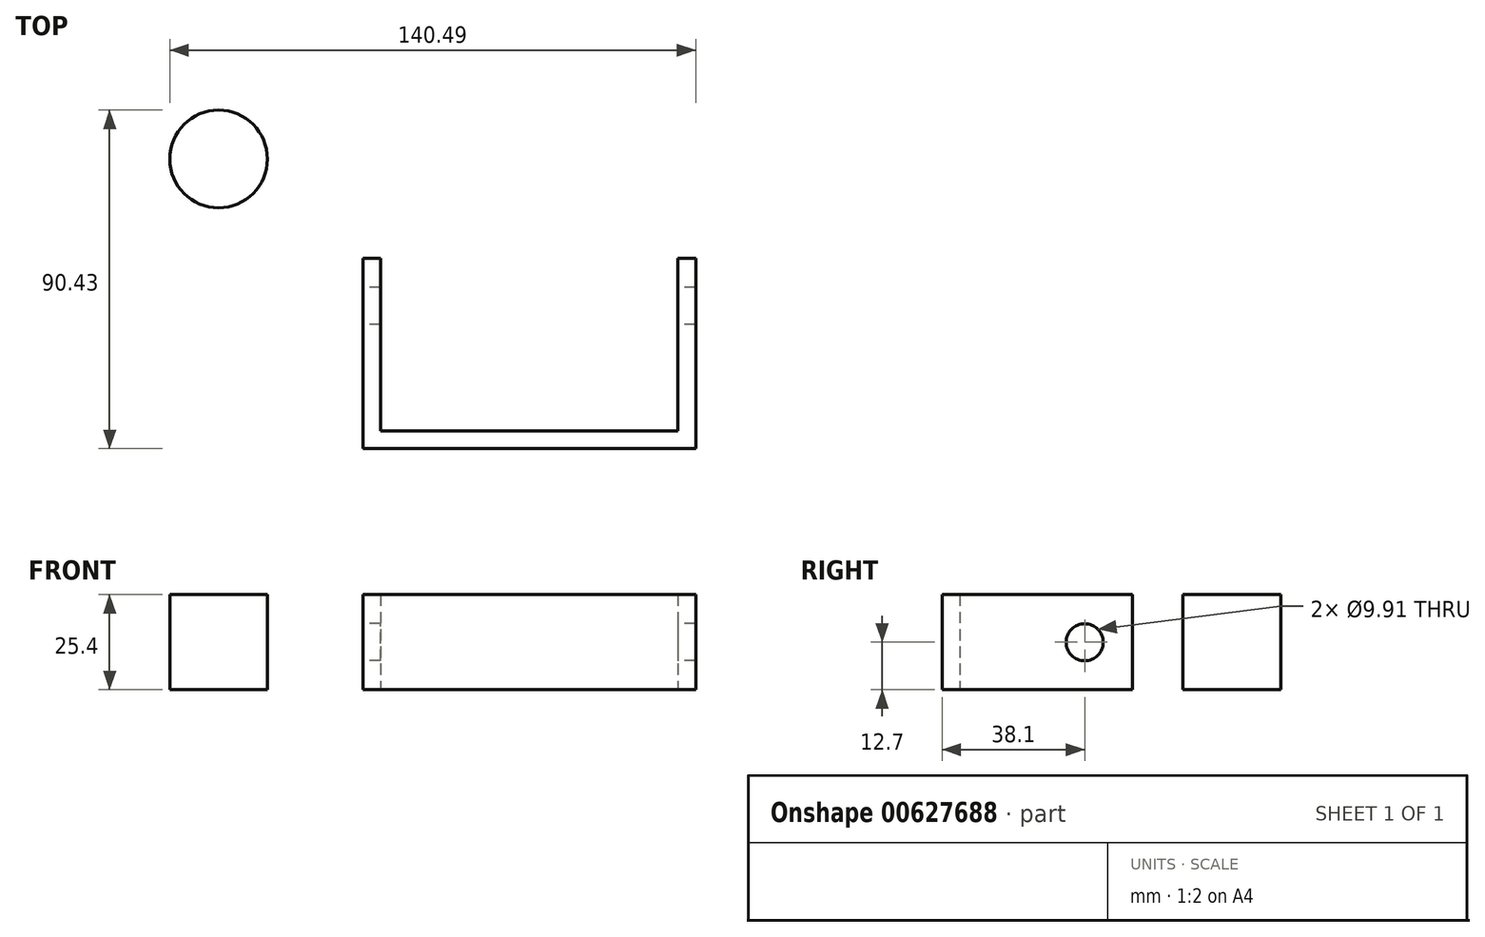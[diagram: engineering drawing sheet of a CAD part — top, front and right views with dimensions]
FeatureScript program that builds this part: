
annotation { "Feature Type Name" : "Feature", "Feature Type Description" : "" }
export const myFeature = defineFeature(function(context is Context, id is Id, definition is map)
    precondition{}
    {
        {
            var Q0;
            Q0=qCreatedBy(makeId("Top.planeOp"),FACE);
            var sketch = newSketch(context, id + "F0", { "sketchPlane" : qUnion([Q0])});
            skLineSegment(sketch, "E0.bottom", {"start": v(44.45, 0) * mm, "end": v(-44.45, 0) * mm});
            skLineSegment(sketch, "E0.top", {"start": v(44.45, 50.8) * mm, "end": v(-44.45, 50.8) * mm, "construction": true});
            skLineSegment(sketch, "E0.left", {"start": v(44.45, 0) * mm, "end": v(44.45, 50.8) * mm});
            skLineSegment(sketch, "E0.right", {"start": v(-44.45, 0) * mm, "end": v(-44.45, 50.8) * mm});
            skPoint(sketch, "E0.middle", {"position": v(0, 25.4) * mm});
            skLineSegment(sketch, "E1", {"start": v(-44.45, 38.1) * mm, "end": v(44.45, 38.1) * mm, "construction": true});
            skLineSegment(sketch, "E2.bottom", {"start": v(-38.1, 63.5) * mm, "end": v(38.1, 63.5) * mm, "construction": true});
            skLineSegment(sketch, "E2.top", {"start": v(-38.1, 12.7) * mm, "end": v(38.1, 12.7) * mm, "construction": true});
            skLineSegment(sketch, "E2.left", {"start": v(-38.1, 63.5) * mm, "end": v(-38.1, 12.7) * mm, "construction": true});
            skLineSegment(sketch, "E2.right", {"start": v(38.1, 63.5) * mm, "end": v(38.1, 12.7) * mm, "construction": true});
            skPoint(sketch, "E2.middle", {"position": v(0, 38.1) * mm});
            skLineSegment(sketch, "E3", {"start": v(-44.45, 50.8) * mm, "end": v(-39.69, 50.8) * mm});
            skLineSegment(sketch, "E4", {"start": v(-39.69, 50.8) * mm, "end": v(-39.69, 4.76) * mm});
            skLineSegment(sketch, "E5", {"start": v(-39.69, 4.76) * mm, "end": v(39.69, 4.76) * mm});
            skLineSegment(sketch, "E6", {"start": v(39.69, 4.76) * mm, "end": v(39.69, 50.8) * mm});
            skLineSegment(sketch, "E7", {"start": v(39.69, 50.8) * mm, "end": v(44.45, 50.8) * mm});
            skSolve(sketch);
        }
        {
            var Q0;
            Q0 = qSketchRegion(id + "F0", true);
            extrude(context, id + "F1", {"entities" : qUnion([Q0]), "depth" : 25.4 * mm, "offsetDistance" : 25.4 * mm});
        }
        {
            var Q0;
            Q0=makeQuery(id+"F1.opExtrude","SWEPT_FACE",FACE,{"disambiguationData":[OSD([sQuery(id+"F0.wireOp",EDGE,"E0.right")])]});
            var sketch = newSketch(context, id + "F2", { "sketchPlane" : qUnion([Q0])});
            skLineSegment(sketch, "E8", {"start": v(0, 12.7) * mm, "end": v(-50.8, 12.7) * mm, "construction": true});
            skCircle(sketch, "E9", {"center": v(-38.1, 12.7) * mm, "radius": 4.95 * mm});
            skSolve(sketch);
        }
        {
            var Q0;
            Q0 = qSketchRegion(id + "F2", true);
            extrude(context, id + "F3", {"entities" : qUnion([Q0]), "operationType" : NewBodyOperationType.REMOVE, "endBound" : BoundingType.THROUGH_ALL, "oppositeDirection" : true, "depth" : 25.4 * mm, "offsetDistance" : 25.4 * mm});
        }
        {
            var Q0;
            Q0=qCreatedBy(makeId("Top.planeOp"),FACE);
            var sketch = newSketch(context, id + "F4", { "sketchPlane" : qUnion([Q0])});
            skCircle(sketch, "E10", {"center": v(-83, 77.38) * mm, "radius": 13.05 * mm});
            skSolve(sketch);
        }
        {
            var Q0;
            Q0 = qSketchRegion(id + "F4", true);
            extrude(context, id + "F5", {"entities" : qUnion([Q0]), "depth" : 25.4 * mm, "offsetDistance" : 25.4 * mm});
        }
    });
